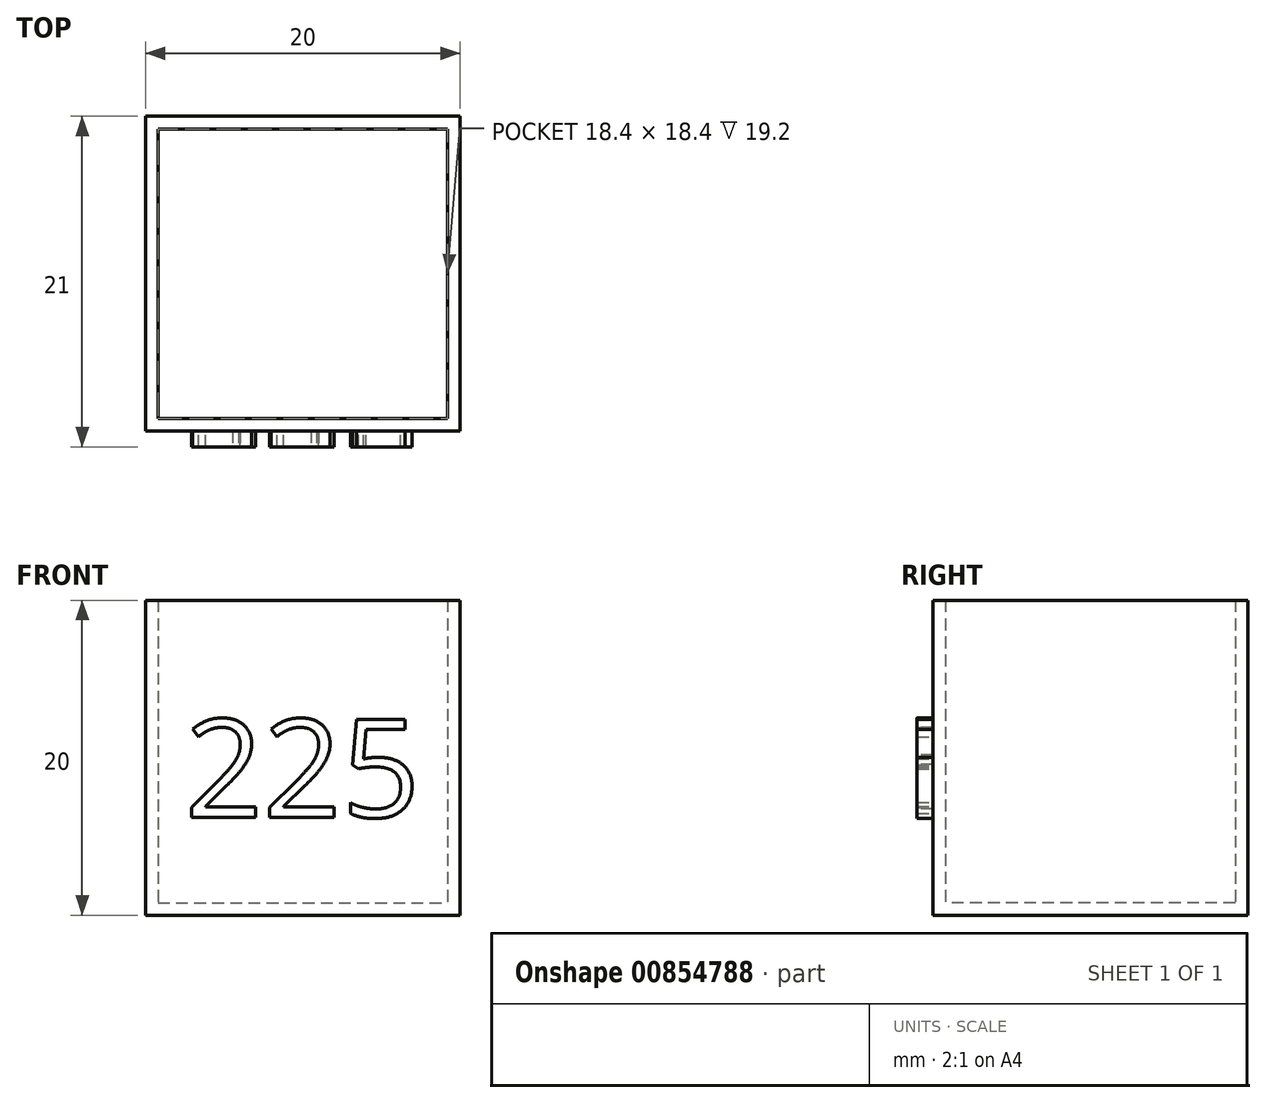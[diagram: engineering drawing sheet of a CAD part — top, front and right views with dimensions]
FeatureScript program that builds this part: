
annotation { "Feature Type Name" : "Feature", "Feature Type Description" : "" }
export const myFeature = defineFeature(function(context is Context, id is Id, definition is map)
    precondition{}
    {
        {
            var Q0;
            Q0=qCreatedBy(makeId("Top.planeOp"),FACE);
            var sketch = newSketch(context, id + "F0", { "sketchPlane" : qUnion([Q0])});
            skLineSegment(sketch, "E0.bottom", {"start": v(-10, 10) * mm, "end": v(10, 10) * mm});
            skLineSegment(sketch, "E0.top", {"start": v(-10, -10) * mm, "end": v(10, -10) * mm});
            skLineSegment(sketch, "E0.left", {"start": v(-10, 10) * mm, "end": v(-10, -10) * mm});
            skLineSegment(sketch, "E0.right", {"start": v(10, 10) * mm, "end": v(10, -10) * mm});
            skSolve(sketch);
        }
        {
            var Q0;
            Q0 = qSketchRegion(id + "F0", true);
            extrude(context, id + "F1", {"entities" : qUnion([Q0]), "depth" : 20 * mm, "offsetDistance" : 25 * mm});
        }
        {
            var Q0;
            Q0=makeQuery(id+"F1.opExtrude","CAP_FACE",FACE,{"disambiguationData":[OSD([sQuery(id+"F0.wireOp",EDGE,"E0.bottom"),sQuery(id+"F0.wireOp",EDGE,"E0.top"),sQuery(id+"F0.wireOp",EDGE,"E0.left"),sQuery(id+"F0.wireOp",EDGE,"E0.right")])],"isStart":false});
            shell(context, id + "F2", {"entities" : qUnion([Q0]), "thickness" : .8 * mm});
        }
        {
            var Q0;
            Q0=makeQuery(id+"F1.opExtrude","SWEPT_FACE",FACE,{"disambiguationData":[OSD([sQuery(id+"F0.wireOp",EDGE,"E0.top")])]});
            var sketch = newSketch(context, id + "F3", { "sketchPlane" : qUnion([Q0])});
            skText(sketch, "E1", { "text": "225", "fontName": "OpenSans-Regular.ttf"});
            const initialGuessF3  = {"E1": [-0.0075, 0.00623, 1, 0, 0.00627]};
            skSetInitialGuess(sketch, initialGuessF3);
            skSolve(sketch);
        }
        {
            var Q0;
            Q0 = qSketchRegion(id + "F3", true);
            extrude(context, id + "F4", {"entities" : qUnion([Q0]), "operationType" : NewBodyOperationType.ADD, "depth" : 1 * mm, "offsetDistance" : 25 * mm});
        }
    });
